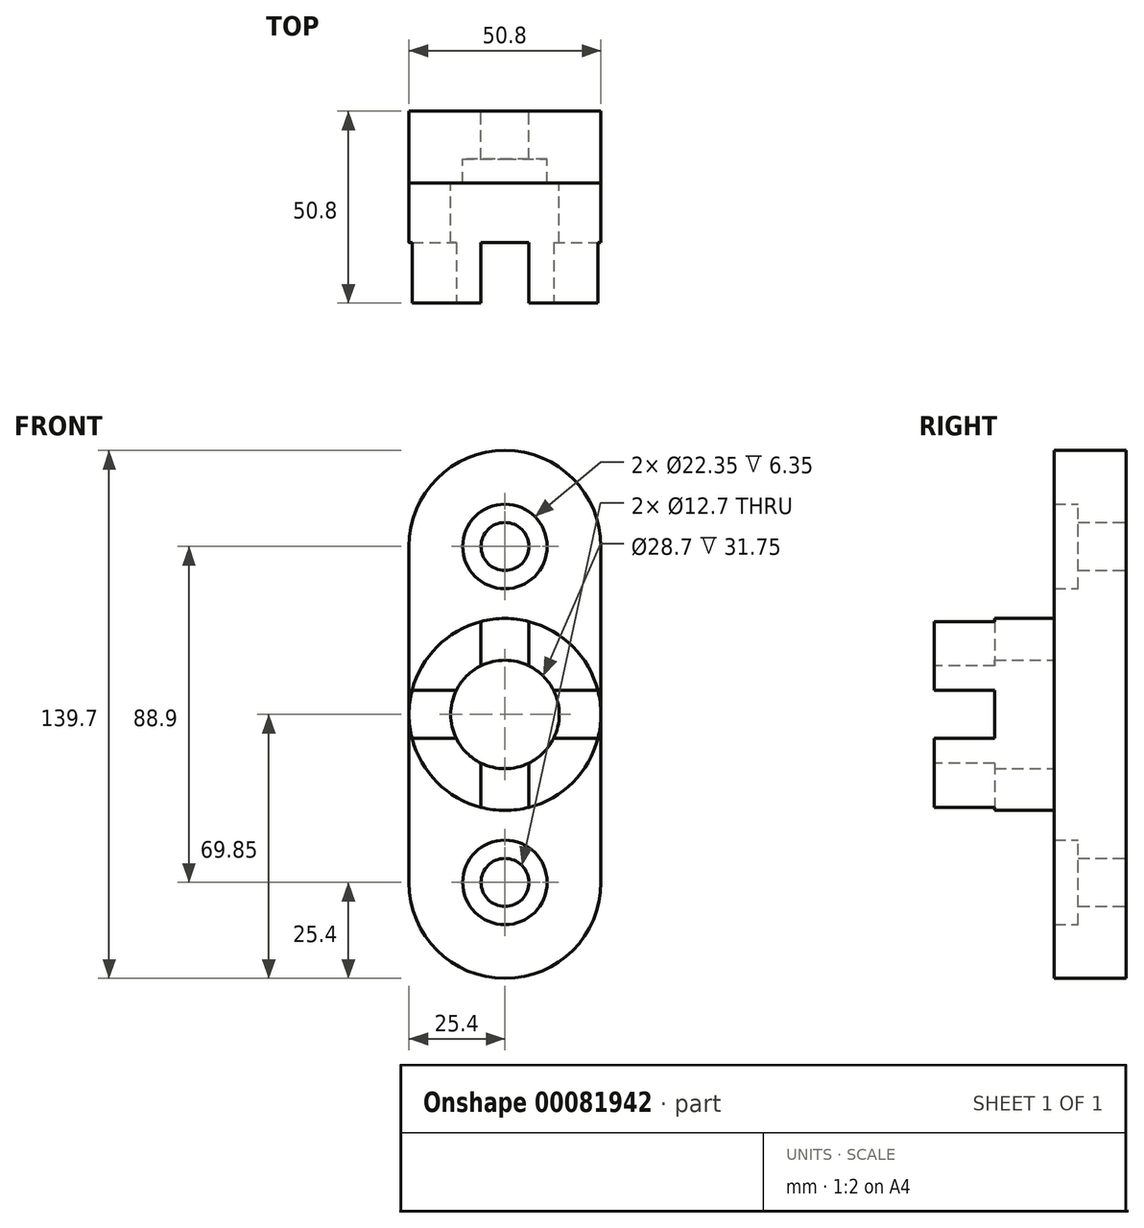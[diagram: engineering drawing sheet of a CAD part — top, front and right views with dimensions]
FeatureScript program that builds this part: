
annotation { "Feature Type Name" : "Feature", "Feature Type Description" : "" }
export const myFeature = defineFeature(function(context is Context, id is Id, definition is map)
    precondition{}
    {
        {
            var Q0;
            Q0=qCreatedBy(makeId("Front.planeOp"),FACE);
            var sketch = newSketch(context, id + "F0", { "sketchPlane" : qUnion([Q0])});
            skLineSegment(sketch, "E0", {"start": v(0, 0) * mm, "end": v(0, -44.45) * mm, "construction": true});
            skLineSegment(sketch, "E1", {"start": v(0, 0) * mm, "end": v(0, 44.45) * mm, "construction": true});
            skCircle(sketch, "E2", {"center": v(0, -44.45) * mm, "radius": 6.35 * mm});
            skCircle(sketch, "E3", {"center": v(0, -44.45) * mm, "radius": 11.18 * mm});
            skCircle(sketch, "E4", {"center": v(0, 44.45) * mm, "radius": 6.35 * mm});
            skCircle(sketch, "E5", {"center": v(0, 44.45) * mm, "radius": 11.18 * mm});
            skArc(sketch, "E6", {"start": v(0, -69.85) * mm, "mid": v(-17.96, -62.41) * mm, "end": v(-25.4, -44.45) * mm});
            skArc(sketch, "E7", {"start": v(0, -69.85) * mm, "mid": v(17.96, -62.41) * mm, "end": v(25.4, -44.45) * mm});
            skArc(sketch, "E8", {"start": v(0, 69.85) * mm, "mid": v(-17.96, 62.41) * mm, "end": v(-25.4, 44.45) * mm});
            skArc(sketch, "E9", {"start": v(0, 69.85) * mm, "mid": v(17.96, 62.41) * mm, "end": v(25.4, 44.45) * mm});
            skLineSegment(sketch, "E10", {"start": v(-25.4, 44.45) * mm, "end": v(-25.4, -44.45) * mm});
            skLineSegment(sketch, "E11", {"start": v(25.4, 44.45) * mm, "end": v(25.4, -44.45) * mm});
            skSolve(sketch);
        }
        {
            var Q0;
            Q0=makeQuery(id+"F0.imprint","IMPRINT",FACE,{"disambiguationData":[TD([[makeQuery(id+"F0.imprint","IMPRINT",EDGE,{"derivedFrom":sQuery(id+"F0.wireOp",EDGE,"E3")}),-1.0]])]});
            extrude(context, id + "F1", {"entities" : qUnion([Q0]), "depth" : 19.05 * mm});
        }
        {
            var Q0;
            Q0=makeQuery(id+"F0.imprint","IMPRINT",FACE,{"disambiguationData":[TD([[makeQuery(id+"F0.imprint","IMPRINT",EDGE,{"derivedFrom":sQuery(id+"F0.wireOp",EDGE,"E2")}),-1.0]])]});
            var Q1;
            Q1=makeQuery(id+"F0.imprint","IMPRINT",FACE,{"disambiguationData":[TD([[makeQuery(id+"F0.imprint","IMPRINT",EDGE,{"derivedFrom":sQuery(id+"F0.wireOp",EDGE,"E4")}),-1.0]])]});
            extrude(context, id + "F2", {"entities" : qUnion([Q0, Q1]), "operationType" : NewBodyOperationType.ADD, "depth" : 12.7 * mm});
        }
        {
            var Q0;
            Q0=makeQuery(id+"F1.opExtrude","CAP_FACE",FACE,{"disambiguationData":[OSD([sQuery(id+"F0.wireOp",EDGE,"E3"),sQuery(id+"F0.wireOp",EDGE,"E5"),sQuery(id+"F0.wireOp",EDGE,"E6"),sQuery(id+"F0.wireOp",EDGE,"E7"),sQuery(id+"F0.wireOp",EDGE,"E8"),sQuery(id+"F0.wireOp",EDGE,"E9"),sQuery(id+"F0.wireOp",EDGE,"E10"),sQuery(id+"F0.wireOp",EDGE,"E11")])],"isStart":false});
            var sketch = newSketch(context, id + "F3", { "sketchPlane" : qUnion([Q0])});
            skCircle(sketch, "E12", {"center": v(0, 0) * mm, "radius": 14.35 * mm});
            skLineSegment(sketch, "E13", {"start": v(-25.4, 0) * mm, "end": v(25.4, 0) * mm, "construction": true});
            skLineSegment(sketch, "E14", {"start": v(-24.6, -6.35) * mm, "end": v(24.6, -6.35) * mm, "construction": true});
            skLineSegment(sketch, "E15", {"start": v(0, 25.4) * mm, "end": v(0, -25.4) * mm, "construction": true});
            skPoint(sketch, "E15.startSnap0", {"position": v(0, 4.2) * mm});
            skPoint(sketch, "E15.endSnap0", {"position": v(0, -6.35) * mm});
            skLineSegment(sketch, "E16", {"start": v(-25.4, 25.4) * mm, "end": v(25.4, 25.4) * mm, "construction": true});
            skLineSegment(sketch, "E17", {"start": v(-25.4, -25.4) * mm, "end": v(25.4, -25.4) * mm, "construction": true});
            skLineSegment(sketch, "E18", {"start": v(-24.6, 6.35) * mm, "end": v(24.6, 6.35) * mm, "construction": true});
            skLineSegment(sketch, "E19", {"start": v(-6.35, 24.6) * mm, "end": v(-6.35, -24.6) * mm, "construction": true});
            skLineSegment(sketch, "E20", {"start": v(6.35, 24.6) * mm, "end": v(6.35, -24.6) * mm, "construction": true});
            skArc(sketch, "E21", {"start": v(-24.58, 6.4) * mm, "mid": v(-25.4, 0.02) * mm, "end": v(-24.6, -6.35) * mm});
            skArc(sketch, "E22", {"start": v(-24.6, -6.35) * mm, "mid": v(-17.96, -17.96) * mm, "end": v(-6.35, -24.6) * mm});
            skArc(sketch, "E23", {"start": v(24.6, 6.35) * mm, "mid": v(17.96, 17.96) * mm, "end": v(6.35, 24.6) * mm});
            skArc(sketch, "E24", {"start": v(24.67, -6.05) * mm, "mid": v(25.4, 0.15) * mm, "end": v(24.6, 6.35) * mm});
            skArc(sketch, "E25", {"start": v(-6.35, -24.6) * mm, "mid": v(0, -25.4) * mm, "end": v(6.35, -24.6) * mm});
            skArc(sketch, "E26", {"start": v(6.35, -24.6) * mm, "mid": v(18.07, -17.85) * mm, "end": v(24.67, -6.05) * mm});
            skArc(sketch, "E27", {"start": v(6.35, 24.6) * mm, "mid": v(0, 25.4) * mm, "end": v(-6.35, 24.6) * mm});
            skArc(sketch, "E28", {"start": v(-6.35, 24.6) * mm, "mid": v(-17.94, 17.98) * mm, "end": v(-24.58, 6.4) * mm});
            skLineSegment(sketch, "E29", {"start": v(-6.35, -12.87) * mm, "end": v(-6.35, -24.6) * mm});
            skLineSegment(sketch, "E30", {"start": v(6.35, -12.87) * mm, "end": v(6.35, -24.6) * mm});
            skLineSegment(sketch, "E31", {"start": v(12.87, -6.35) * mm, "end": v(24.6, -6.35) * mm});
            skLineSegment(sketch, "E32", {"start": v(12.87, 6.35) * mm, "end": v(24.6, 6.35) * mm});
            skLineSegment(sketch, "E33", {"start": v(-24.6, 6.35) * mm, "end": v(-12.87, 6.35) * mm});
            skLineSegment(sketch, "E34", {"start": v(-24.6, -6.35) * mm, "end": v(-12.87, -6.35) * mm});
            skLineSegment(sketch, "E35", {"start": v(-6.35, 24.6) * mm, "end": v(-6.35, 12.87) * mm});
            skLineSegment(sketch, "E36", {"start": v(6.35, 24.6) * mm, "end": v(6.35, 12.87) * mm});
            skSolve(sketch);
        }
        {
            var Q0;
            Q0 = qSketchRegion(id + "F3", true);
            extrude(context, id + "F4", {"entities" : qUnion([Q0]), "operationType" : NewBodyOperationType.ADD, "depth" : 31.75 * mm});
        }
        {
            var Q0;
            Q0=makeQuery(id+"F4.opExtrude","CAP_FACE",FACE,{"disambiguationData":[OSD([sQuery(id+"F3.wireOp",EDGE,"E12"),sQuery(id+"F3.wireOp",EDGE,"E21"),sQuery(id+"F3.wireOp",EDGE,"E22"),sQuery(id+"F3.wireOp",EDGE,"E23"),sQuery(id+"F3.wireOp",EDGE,"E24"),sQuery(id+"F3.wireOp",EDGE,"E25"),sQuery(id+"F3.wireOp",EDGE,"E26"),sQuery(id+"F3.wireOp",EDGE,"E27"),sQuery(id+"F3.wireOp",EDGE,"E28")])],"isStart":false});
            var sketch = newSketch(context, id + "F5", { "sketchPlane" : qUnion([Q0])});
            skLineSegment(sketch, "E37.0", {"start": v(-6.35, 24.6) * mm, "end": v(-6.35, 12.87) * mm});
            skLineSegment(sketch, "E38.0", {"start": v(6.35, 24.6) * mm, "end": v(6.35, 12.87) * mm});
            skArc(sketch, "E39.0", {"start": v(6.35, 24.6) * mm, "mid": v(0, 25.4) * mm, "end": v(-6.35, 24.6) * mm});
            skArc(sketch, "E40.0", {"start": v(-24.58, 6.4) * mm, "mid": v(-25.4, 0.02) * mm, "end": v(-24.6, -6.35) * mm});
            skLineSegment(sketch, "E41.0", {"start": v(-24.6, 6.35) * mm, "end": v(-12.87, 6.35) * mm});
            skLineSegment(sketch, "E42.0", {"start": v(-24.6, -6.35) * mm, "end": v(-12.87, -6.35) * mm});
            skLineSegment(sketch, "E43.0", {"start": v(6.35, -12.87) * mm, "end": v(6.35, -24.6) * mm});
            skLineSegment(sketch, "E44.0", {"start": v(-6.35, -12.87) * mm, "end": v(-6.35, -24.6) * mm});
            skArc(sketch, "E45.0", {"start": v(-6.35, -24.6) * mm, "mid": v(0, -25.4) * mm, "end": v(6.35, -24.6) * mm});
            skLineSegment(sketch, "E46.0", {"start": v(12.87, -6.35) * mm, "end": v(24.6, -6.35) * mm});
            skLineSegment(sketch, "E47.0", {"start": v(12.87, 6.35) * mm, "end": v(24.6, 6.35) * mm});
            skArc(sketch, "E48.0", {"start": v(24.67, -6.05) * mm, "mid": v(25.4, 0.15) * mm, "end": v(24.6, 6.35) * mm});
            skSolve(sketch);
        }
        {
            var Q0;
            {var subQ0=sQuery(id+"F5.wireOp",EDGE,"E46.0");Q0=makeQuery(id+"F5.imprint","IMPRINT",FACE,{"disambiguationData":[TD([[makeQuery(id+"F5.imprint","IMPRINT",EDGE,{"derivedFrom":subQ0}),1.0]])]});}
            var Q1;
            {var subQ2=sQuery(id+"F5.wireOp",EDGE,"E41.0");Q1=makeQuery(id+"F5.imprint","IMPRINT",FACE,{"disambiguationData":[TD([[makeQuery(id+"F5.imprint","IMPRINT",EDGE,{"derivedFrom":subQ2}),-1.0]])]});}
            var Q2;
            {var subQ0=sQuery(id+"F5.wireOp",EDGE,"E43.0");Q2=makeQuery(id+"F5.imprint","IMPRINT",FACE,{"disambiguationData":[TD([[makeQuery(id+"F5.imprint","IMPRINT",EDGE,{"derivedFrom":subQ0}),-1.0]])]});}
            var Q3;
            {var subQ0=sQuery(id+"F5.wireOp",EDGE,"E37.0");Q3=makeQuery(id+"F5.imprint","IMPRINT",FACE,{"disambiguationData":[TD([[makeQuery(id+"F5.imprint","IMPRINT",EDGE,{"derivedFrom":subQ0}),1.0]])]});}
            extrude(context, id + "F6", {"entities" : qUnion([Q0, Q1, Q2, Q3]), "operationType" : NewBodyOperationType.REMOVE, "oppositeDirection" : true, "depth" : 16 * mm});
        }
    });
